# Revit family: PIBA
name_source: partatom
category: Structural Connections
revit_build: Autodesk Revit 2015 (Build: 20140606_1530(x64)
units: mm (PartAtom-declared; Revit-internal decimal feet)

## types (1)
- PIBA
    Default Elevation = 0 mm  [stored 0 ft]
    Density = 0.00 kg
    Description = Concealed beam hanger
    EPD = https://www.strongtie.eu
    ETA / DoP = https://www.strongtie.eu
    Manufacturer = Simpson Strong-Tie
    Model = PIBA
    Model Disclaimer = Contact Simpson Strong-Tie Company  for more information
    Name = PIBA
    ObjectType = PIBA
    Product Material = Galvanised
    Product Type = Concealed beam hanger
    Reference = PIPA
    STD type1 = STD8X80G-B
    STD type2 = STD8X115G-B
    STD type3 = STD8X140G-B
    Technical datasheet = https://www.strongtie.eu
    URL = www.strongtie.eu

note: [stored X ft] marks values corroborated as IEEE doubles in the binary element streams (Revit-internal decimal feet)

## geometry (parser evidence)
native form markers: Blend x29, Sweep x11
no freeform markers — native parametric forms only
